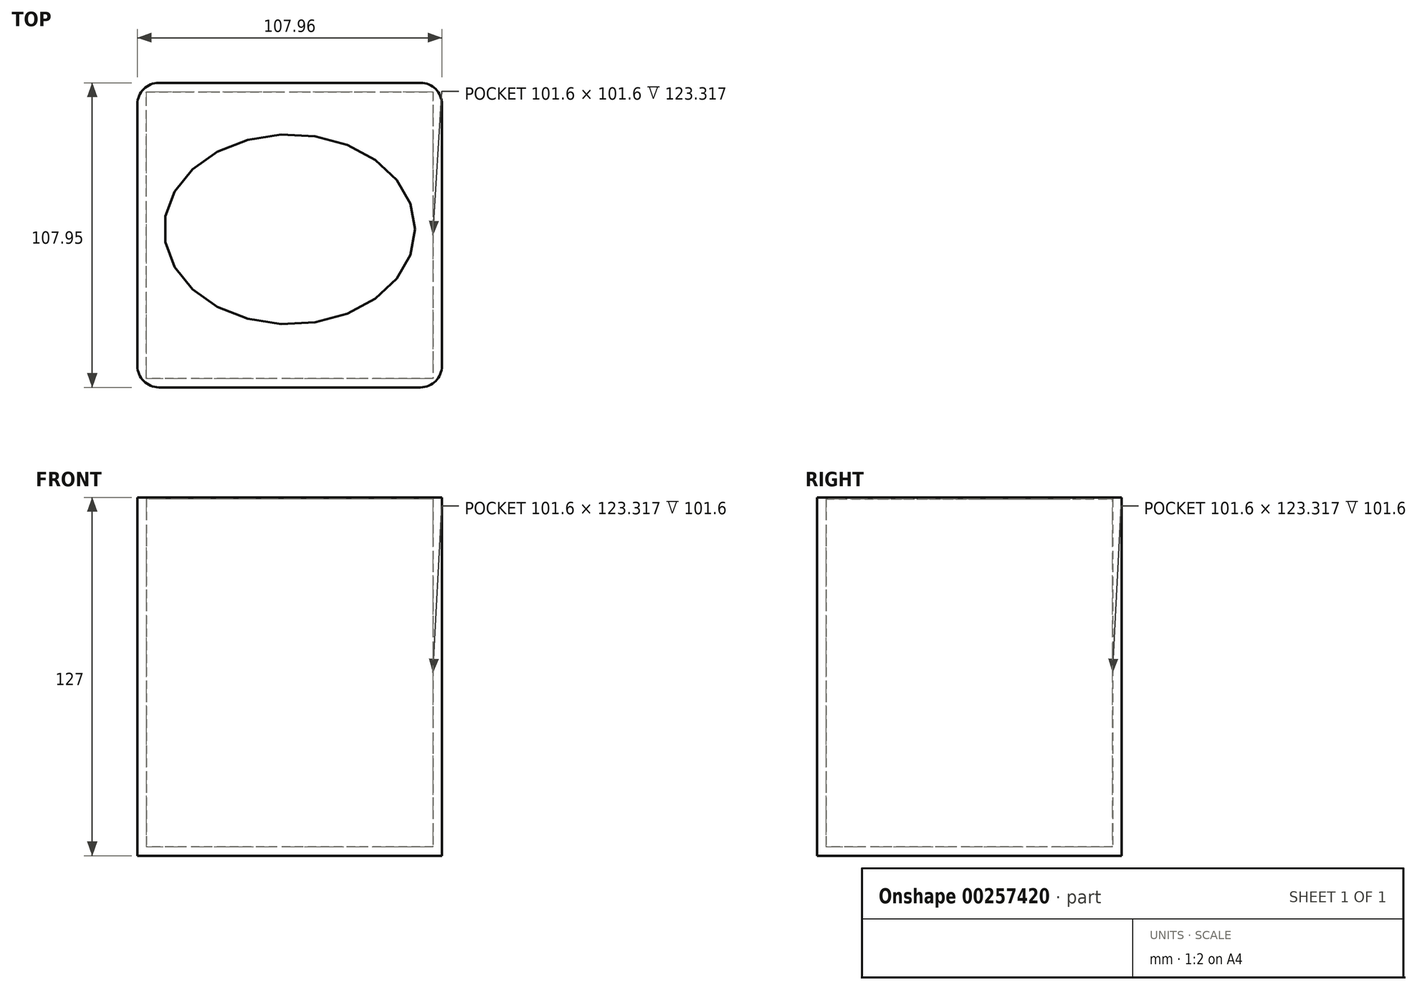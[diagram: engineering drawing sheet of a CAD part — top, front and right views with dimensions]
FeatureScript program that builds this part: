
annotation { "Feature Type Name" : "Feature", "Feature Type Description" : "" }
export const myFeature = defineFeature(function(context is Context, id is Id, definition is map)
    precondition{}
    {
        {
            var Q0;
            Q0=qCreatedBy(makeId("Top.planeOp"),FACE);
            var sketch = newSketch(context, id + "F0", { "sketchPlane" : qUnion([Q0])});
            skLineSegment(sketch, "E0", {"start": v(0, -56.03) * mm, "end": v(-53.98, -56.03) * mm});
            skLineSegment(sketch, "E1", {"start": v(-53.98, -56.03) * mm, "end": v(-53.98, 51.92) * mm});
            skLineSegment(sketch, "E2", {"start": v(-53.98, 51.92) * mm, "end": v(53.97, 51.92) * mm});
            skLineSegment(sketch, "E3", {"start": v(53.97, 51.92) * mm, "end": v(53.97, -56.03) * mm});
            skLineSegment(sketch, "E4", {"start": v(53.97, -56.03) * mm, "end": v(0, -56.03) * mm});
            skLineSegment(sketch, "E5", {"start": v(0, -56.03) * mm, "end": v(0, -52.85) * mm});
            skLineSegment(sketch, "E6", {"start": v(0, -52.85) * mm, "end": v(-50.8, -52.85) * mm});
            skLineSegment(sketch, "E7", {"start": v(-50.8, -52.85) * mm, "end": v(-50.8, 48.75) * mm});
            skLineSegment(sketch, "E8", {"start": v(-50.8, 48.75) * mm, "end": v(50.8, 48.75) * mm});
            skLineSegment(sketch, "E9", {"start": v(50.8, 48.75) * mm, "end": v(50.8, -52.85) * mm});
            skLineSegment(sketch, "E10", {"start": v(50.8, -52.85) * mm, "end": v(0, -52.85) * mm});
            skSolve(sketch);
        }
        {
            var Q0;
            Q0 = qSketchRegion(id + "F0", true);
            extrude(context, id + "F1", {"entities" : qUnion([Q0]), "depth" : 127 * mm});
        }
        {
            var Q0;
            Q0=makeQuery(id+"F0.imprint","IMPRINT",FACE,{"disambiguationData":[TD([[makeQuery(id+"F0.imprint","IMPRINT",EDGE,{"derivedFrom":sQuery(id+"F0.wireOp",EDGE,"E6")}),-1.0]])]});
            extrude(context, id + "F2", {"entities" : qUnion([Q0]), "operationType" : NewBodyOperationType.ADD, "depth" : 3.17 * mm});
        }
        {
            var Q0;
            Q0=makeQuery(id+"F1.opExtrude","CAP_FACE",FACE,{"disambiguationData":[OSD([sQuery(id+"F0.wireOp",EDGE,"E0"),sQuery(id+"F0.wireOp",EDGE,"E1"),sQuery(id+"F0.wireOp",EDGE,"E2"),sQuery(id+"F0.wireOp",EDGE,"E3"),sQuery(id+"F0.wireOp",EDGE,"E4"),sQuery(id+"F0.wireOp",EDGE,"E6"),sQuery(id+"F0.wireOp",EDGE,"E7"),sQuery(id+"F0.wireOp",EDGE,"E8"),sQuery(id+"F0.wireOp",EDGE,"E9"),sQuery(id+"F0.wireOp",EDGE,"E10")])],"isStart":false});
            var sketch = newSketch(context, id + "F3", { "sketchPlane" : qUnion([Q0])});
            skLineSegment(sketch, "E11", {"start": v(-50.8, 48.75) * mm, "end": v(50.8, 48.75) * mm});
            skLineSegment(sketch, "E12", {"start": v(50.8, 48.75) * mm, "end": v(50.8, -52.85) * mm});
            skLineSegment(sketch, "E13", {"start": v(50.8, -52.85) * mm, "end": v(-50.8, -52.85) * mm});
            skLineSegment(sketch, "E14", {"start": v(-50.8, -52.85) * mm, "end": v(-50.8, 48.75) * mm});
            skSolve(sketch);
        }
        {
            var Q0;
            Q0 = qSketchRegion(id + "F3", true);
            extrude(context, id + "F4", {"entities" : qUnion([Q0]), "operationType" : NewBodyOperationType.ADD, "oppositeDirection" : true, "depth" : 0.5 * mm});
        }
        {
            var Q0;
            Q0=makeQuery(id+"F4.boolean.opBoolean","MERGE",FACE,{"derivedFrom":[makeQuery(id+"F1.opExtrude","CAP_FACE",FACE,{"disambiguationData":[OSD([sQuery(id+"F0.wireOp",EDGE,"E0"),sQuery(id+"F0.wireOp",EDGE,"E1"),sQuery(id+"F0.wireOp",EDGE,"E2"),sQuery(id+"F0.wireOp",EDGE,"E3"),sQuery(id+"F0.wireOp",EDGE,"E4"),sQuery(id+"F0.wireOp",EDGE,"E6"),sQuery(id+"F0.wireOp",EDGE,"E7"),sQuery(id+"F0.wireOp",EDGE,"E8"),sQuery(id+"F0.wireOp",EDGE,"E9"),sQuery(id+"F0.wireOp",EDGE,"E10")])],"isStart":false}),makeQuery(id+"F4.opExtrude","CAP_FACE",FACE,{"disambiguationData":[OSD([sQuery(id+"F3.wireOp",EDGE,"E11"),sQuery(id+"F3.wireOp",EDGE,"E12"),sQuery(id+"F3.wireOp",EDGE,"E13"),sQuery(id+"F3.wireOp",EDGE,"E14")])],"isStart":true})]});
            var sketch = newSketch(context, id + "F5", { "sketchPlane" : qUnion([Q0])});
            skEllipse(sketch, "E15", {"center": v(0, 0) * mm, "majorRadius": 44.45 * mm, "minorRadius": 33.66 * mm, "majorAxis": v(1, 0)});
            skSolve(sketch);
        }
        {
            var Q0;
            Q0=makeQuery(id+"F5.imprint","IMPRINT",FACE,{"disambiguationData":[TD([[makeQuery(id+"F5.imprint","IMPRINT",EDGE,{"derivedFrom":sQuery(id+"F5.wireOp",EDGE,"E15")}),1.0]])]});
            extrude(context, id + "F6", {"entities" : qUnion([Q0]), "operationType" : NewBodyOperationType.REMOVE, "oppositeDirection" : true, "depth" : 12.7 * mm});
        }
        {
            var Q0;
            Q0=makeQuery(id+"F1.opExtrude","SWEPT_EDGE",EDGE,{"disambiguationData":[OSD([sQuery(id+"F0.wireOp",EDGE,"E0"),sQuery(id+"F0.wireOp",EDGE,"E1")])]});
            var Q1;
            Q1=makeQuery(id+"F1.opExtrude","SWEPT_EDGE",EDGE,{"disambiguationData":[OSD([sQuery(id+"F0.wireOp",EDGE,"E1"),sQuery(id+"F0.wireOp",EDGE,"E2")])]});
            var Q2;
            Q2=makeQuery(id+"F1.opExtrude","SWEPT_EDGE",EDGE,{"disambiguationData":[OSD([sQuery(id+"F0.wireOp",EDGE,"E2"),sQuery(id+"F0.wireOp",EDGE,"E3")])]});
            var Q3;
            Q3=makeQuery(id+"F1.opExtrude","SWEPT_EDGE",EDGE,{"disambiguationData":[OSD([sQuery(id+"F0.wireOp",EDGE,"E3"),sQuery(id+"F0.wireOp",EDGE,"E4")])]});
            fillet(context, id + "F7", {"entities" : qUnion([Q0, Q1, Q2, Q3]), "radius" : 7.62 * mm, "allowEdgeOverflow" : false});
        }
    });
